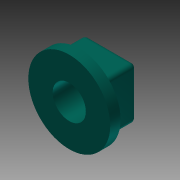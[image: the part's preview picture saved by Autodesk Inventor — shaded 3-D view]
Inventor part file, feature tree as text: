
AUTODESK INVENTOR PART (.ipt)
format: ipt  version: 2013 (Build 170138000, 138)  size: 111,616 bytes
history: native  units: in
note: dims shown in document units (in); Inventor stores cm internally (conversion verified against a paired STEP export)
features: sketch x3, extrude x2, fillet x1, hole x1
ambient origin geometry x8: Origin, YZ Plane, XZ Plane, XY Plane, X Axis, Y Axis, Z Axis, Center Point
bodies: Solid1 (feature_tree)
feature tree (7):
  extrude  "Extrusion1"  Depth=0.05in TaperAngle=0.0deg
  extrude  "Extrusion2"  Depth=0.15in TaperAngle=0.0deg
  fillet  "Fillet1"  Radius=0.02in
  hole  "Hole1"  [1 undecoded]
  sketch  "Sketch1"  dims[d0=0.395in d1=0.05in d2=0.0in]
  sketch  "Sketch2"  dims[d3=0.248in d4=0.15in d5=0.0in d6=0.02in]
  sketch  "Sketch3"  dims[d7=0.16in d8=0.75in d9=0.375in d10=0.25in d11=0.5635in d12=1.0in d13=0.8108in]
note: 1 required parameter value undecoded (feature->parameter linkage not recoverable at this tier; creation-order binding heuristic only, values carry confidence <= 0.55)
